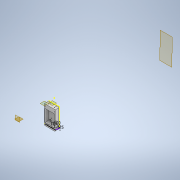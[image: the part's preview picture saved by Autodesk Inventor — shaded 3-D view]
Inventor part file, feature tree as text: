
AUTODESK INVENTOR PART (.ipt)
format: ipt  version: 2022 (Build 260153000, 153)  size: 542,720 bytes
history: native  units: in
note: dims shown in document units (in); Inventor stores cm internally (conversion verified against a paired STEP export)
features: sketch x23, extrude x20, projected_geometry x15, plane x7, fillet x6, sweep x1
ambient origin geometry x8: Origin, YZ Plane, XZ Plane, XY Plane, X Axis, Y Axis, Z Axis, Center Point
bodies: Solid1 (feature_tree)
feature tree (72):
  extrude  "Extrusion1"  Depth=2.2in
  extrude  "Extrusion2"  Depth=0.125in
  extrude  "Extrusion3"  Depth=0.7in TaperAngle=0.0deg
  extrude  "Extrusion4"  Depth=0.4in
  sketch  "Sketch5"  dims[d14=0.4in d15=0.12in]
  plane  "Work Plane1"
  sweep  "Sweep2"
  extrude  "Extrusion5"  Depth=0.4in
  plane  "Work Plane6"
  extrude  "Extrusion6"  Depth=0.0625in
  plane  "Work Plane2"
  plane  "Work Plane3"
  plane  "Work Plane4"
  plane  "Work Plane5"
  extrude  "Extrusion7"  Depth=0.0625in
  extrude  "Extrusion8"  Depth=0.125in
  extrude  "Extrusion9"  TaperAngle=0.0deg  [1 undecoded]
  sketch  "Sketch12"  dims[d36=2.1in d37=1.05in]
  extrude  "Extrusion10"  Depth=1.0in TaperAngle=0.0deg
  extrude  "Extrusion11"  Depth=1.05in
  extrude  "Extrusion12"  Depth=2.8in
  sketch  "Sketch13"  dims[d38=1.0in d39=0.0in d40=2.8in]
  extrude  "Extrusion13"  Depth=0.1in TaperAngle=0.0deg
  extrude  "Extrusion14"  Depth=0.125in
  fillet  "Fillet2"  Radius=1.0in
  fillet  "Fillet3"  Radius=0.12in
  fillet  "Fillet4"  Radius=0.12in
  fillet  "Fillet5"  [1 undecoded]
  extrude  "Extrusion15"  Depth=0.4in
  extrude  "Extrusion16"  Depth=0.8in
  sketch  "Sketch18"  dims[d59=1.0in d60=0.0in d61=1.0in d62=0.0in]
  fillet  "Fillet6"  Radius=0.12in
  sketch  "Sketch19"  dims[d63=0.125in d64=0.125in d65=0.125in]
  plane  "Work Plane10"
  extrude  "Extrusion18"  Depth=1.0in TaperAngle=0.0deg
  extrude  "Extrusion19"  Depth=0.125in
  fillet  "Fillet7"  Radius=0.125in
  extrude  "Extrusion20"  Depth=0.2in
  extrude  "Extrusion21"  Depth=0.5in
  sketch  "Sketch1"  dims[d1=2.5in d2=2.2in]
  sketch  "Sketch2"  dims[d3=0.825in d4=0.0in d5=0.125in]
  projected_geometry  "Projected Loop1"
  sketch  "Sketch3"  dims[d6=0.7in d7=0.0in d8=1.0in d9=0.0in]
  projected_geometry  "Projected Loop2"
  sketch  "Sketch4"  dims[d11=0.4in d13=0.12in]
  sketch  "Sketch6"  dims[d16=1.0in d17=0.0in d18=0.4in]
  sketch  "Sketch7"  dims[d19=30.0in d22=0.0625in]
  projected_geometry  "Projected Loop3"
  sketch  "Sketch8"  dims[d23=0.125in d26=0.0625in]
  projected_geometry  "Projected Loop4"
  sketch  "Sketch9"  dims[d27=0.3in d28=0.125in]
  sketch  "Sketch10"  dims[d29=0.6in d30=0.0in d31=0.0in]
  projected_geometry  "Projected Loop5"
  projected_geometry  "Projected Loop6"
  projected_geometry  "Projected Loop7"
  sketch  "Sketch11"  dims[d32=1.0in d33=0.0in d34=1.0in d35=0.0in]
  projected_geometry  "Projected Loop8"
  projected_geometry  "Projected Loop9"
  sketch  "Sketch14"  dims[d41=1.0in d42=0.0in d43=0.1in d44=0.0in]
  projected_geometry  "Projected Loop10"
  sketch  "Sketch15"  dims[d45=0.8in d46=0.125in d47=1.0in d48=0.0in d49=0.12in d50=0.12in d51=0.0in d52=0.0in]
  projected_geometry  "Projected Loop11"
  sketch  "Sketch16"  dims[d53=1.0in d54=0.0in d55=0.4in]
  projected_geometry  "Projected Loop12"
  sketch  "Sketch17"  dims[d56=0.8in d57=0.12in d58=0.12in]
  sketch  "Sketch20"  dims[d66=0.125in d67=0.2in]
  sketch  "Sketch22"  dims[d68=1.0in d69=0.0in d70=0.5in]
  projected_geometry  "Projected Loop13"
  sketch  "Sketch23"  dims[d71=0.3in]
  projected_geometry  "Projected Loop14"
  sketch  "Sketch24"  dims[d72=0.12in d73=0.12in d74=1.0in d75=0.0in d78=0.125in d79=0.0in d80=0.0in d82=0.325in d83=0.0in d84=0.125in d85=0.35in d89=0.25in d90=0.975in d91=0.625in d92=0.0875in d93=0.0875in d94=0.0875in d97=0.0875in d98=0.0625in d99=0.0in d100=3.0in d101=0.12in d102=2.934in d103=0.556in d104=0.5in d105=0.0in]
  projected_geometry  "Projected Loop15"
note: 2 required parameter values undecoded (feature->parameter linkage not recoverable at this tier; creation-order binding heuristic only, values carry confidence <= 0.55)
